# Revit family: HERZ-TS-90-V Thermostatic Valve Angle Model 7724
name_source: partatom
category: Rohrzubehör
revit_build: Autodesk Revit 2018 (Build: 20190510_1515(x64)
units: mm (PartAtom-declared; Revit-internal decimal feet)

## family parameters
Arbeitsebenenbasiert = Nein
Beim Laden mit Abzugskörper schneiden = Nein
Bemaßung runder Anschluss = Durchmesser verwenden
Gemeinsam genutzt = Nein
Immer vertikal = Ja
OmniClass-Nummer = 23.65.55.14
OmniClass-Titel = Valves for Liquid Services
Teiletyp = Unterbricht

## types (16) — shared parameters
Application = Water heating systems in which hydraulic balancing via return valves is not possible or not desired.
Body = nickel plated
Connection thread for thermostatic head = M28x1.5
H04 = 4.5 mm  [stored 0.0147638 ft]
H06 = 17 mm
H07 = 6.65 mm  [stored 0.0218176 ft]
Hersteller = HERZ Armaturen Ges.m.b.H.
L05 = 12.5 mm  [stored 0.0410105 ft]
Max. operating pressure = 1000000.0 Pa
Max. operating temperature = 110 °C
Medium = Heating water purity according to Austrian standard ÖNORM H 5195 and/or VDI-guideline 2035.
Model = All models are nickel plated and supplied with a red screw cap.
R01 = 14 mm  [stored 0.0459318 ft]
R02 = 10.5 mm  [stored 0.0344488 ft]
R03 = 5.3 mm  [stored 0.0173885 ft]
R04 = 7 mm  [stored 0.0229659 ft]
R05 = 3 mm  [stored 0.00984252 ft]
R06 = 16.15 mm  [stored 0.0529856 ft]
S01 = 10 mm  [stored 0.0328084 ft]
S04 = 45 mm  [stored 0.147638 ft]
SCRNCODE = 05;00;02
SCRNSEQ = ARM;ARM_TYP="ALLF";2
Screw cap = plastic, red
URL = www.herzvalves.com

## per-type parameters (varying)
| type | Part number TH | TH_Kopf_7230 | TH_Kopf_7260 | TH_Kopf_9200_03 | TH_Kopf_9200_06 | TH_Kopf_9200_13 | TH_Kopf_9200_16 | TH_Kopf_9200_30 | TH_Kopf_9200_60 | TH_Kopf_9230 | TH_Kopf_9260 | TH_Kopf_9330_10000mm | TH_Kopf_9330_2000mm | TH_Kopf_9330_5000mm | TH_Kopf_9330_8000mm | TH_Kopf_9860 |
| without thermostatic head | 0 | Nein | Nein | Nein | Nein | Nein | Nein | Nein | Nein | Nein | Nein | Nein | Nein | Nein | Nein | Nein |
| with thermostatic head_7230 | 1723006 | Ja | Nein | Nein | Nein | Nein | Nein | Nein | Nein | Nein | Nein | Nein | Nein | Nein | Nein | Nein |
| with thermostatic head_7260 | 1726006 | Nein | Ja | Nein | Nein | Nein | Nein | Nein | Nein | Nein | Nein | Nein | Nein | Nein | Nein | Nein |
| with thermostatic head_9200_03 | 1920003 | Nein | Nein | Ja | Nein | Nein | Nein | Nein | Nein | Nein | Nein | Nein | Nein | Nein | Nein | Nein |
| with thermostatic head_9200_06 | 1920006 | Nein | Nein | Nein | Ja | Nein | Nein | Nein | Nein | Nein | Nein | Nein | Nein | Nein | Nein | Nein |
| with thermostatic head_9200_13 | 1920013 | Nein | Nein | Nein | Nein | Ja | Nein | Nein | Nein | Nein | Nein | Nein | Nein | Nein | Nein | Nein |
| with thermostatic head_9200_16 | 1920016 | Nein | Nein | Nein | Nein | Nein | Ja | Nein | Nein | Nein | Nein | Nein | Nein | Nein | Nein | Nein |
| with thermostatic head_9200_30 | 1920030 | Nein | Nein | Nein | Nein | Nein | Nein | Ja | Nein | Nein | Nein | Nein | Nein | Nein | Nein | Nein |
| with thermostatic head_9200_60 | 1920060 | Nein | Nein | Nein | Nein | Nein | Nein | Nein | Ja | Nein | Nein | Nein | Nein | Nein | Nein | Nein |
| with thermostatic head_9230 | 1923006 | Nein | Nein | Nein | Nein | Nein | Nein | Nein | Nein | Ja | Nein | Nein | Nein | Nein | Nein | Nein |
| with thermostatic head_9260 | 1926006 | Nein | Nein | Nein | Nein | Nein | Nein | Nein | Nein | Nein | Ja | Nein | Nein | Nein | Nein | Nein |
| with thermostatic head_9330_10000mm | 1933020 | Nein | Nein | Nein | Nein | Nein | Nein | Nein | Nein | Nein | Nein | Ja | Nein | Nein | Nein | Nein |
| with thermostatic head_9330_2000mm | 1933005 | Nein | Nein | Nein | Nein | Nein | Nein | Nein | Nein | Nein | Nein | Nein | Ja | Nein | Nein | Nein |
| with thermostatic head_9330_5000mm | 1933010 | Nein | Nein | Nein | Nein | Nein | Nein | Nein | Nein | Nein | Nein | Nein | Nein | Ja | Nein | Nein |
| with thermostatic head_9330_8000mm | 1933018 | Nein | Nein | Nein | Nein | Nein | Nein | Nein | Nein | Nein | Nein | Nein | Nein | Nein | Ja | Nein |
| with thermostatic head_9860 | 1986010 | Nein | Nein | Nein | Nein | Nein | Nein | Nein | Nein | Nein | Nein | Nein | Nein | Nein | Nein | Ja |

note: [stored X ft] marks values corroborated as IEEE doubles in the binary element streams (Revit-internal decimal feet)
